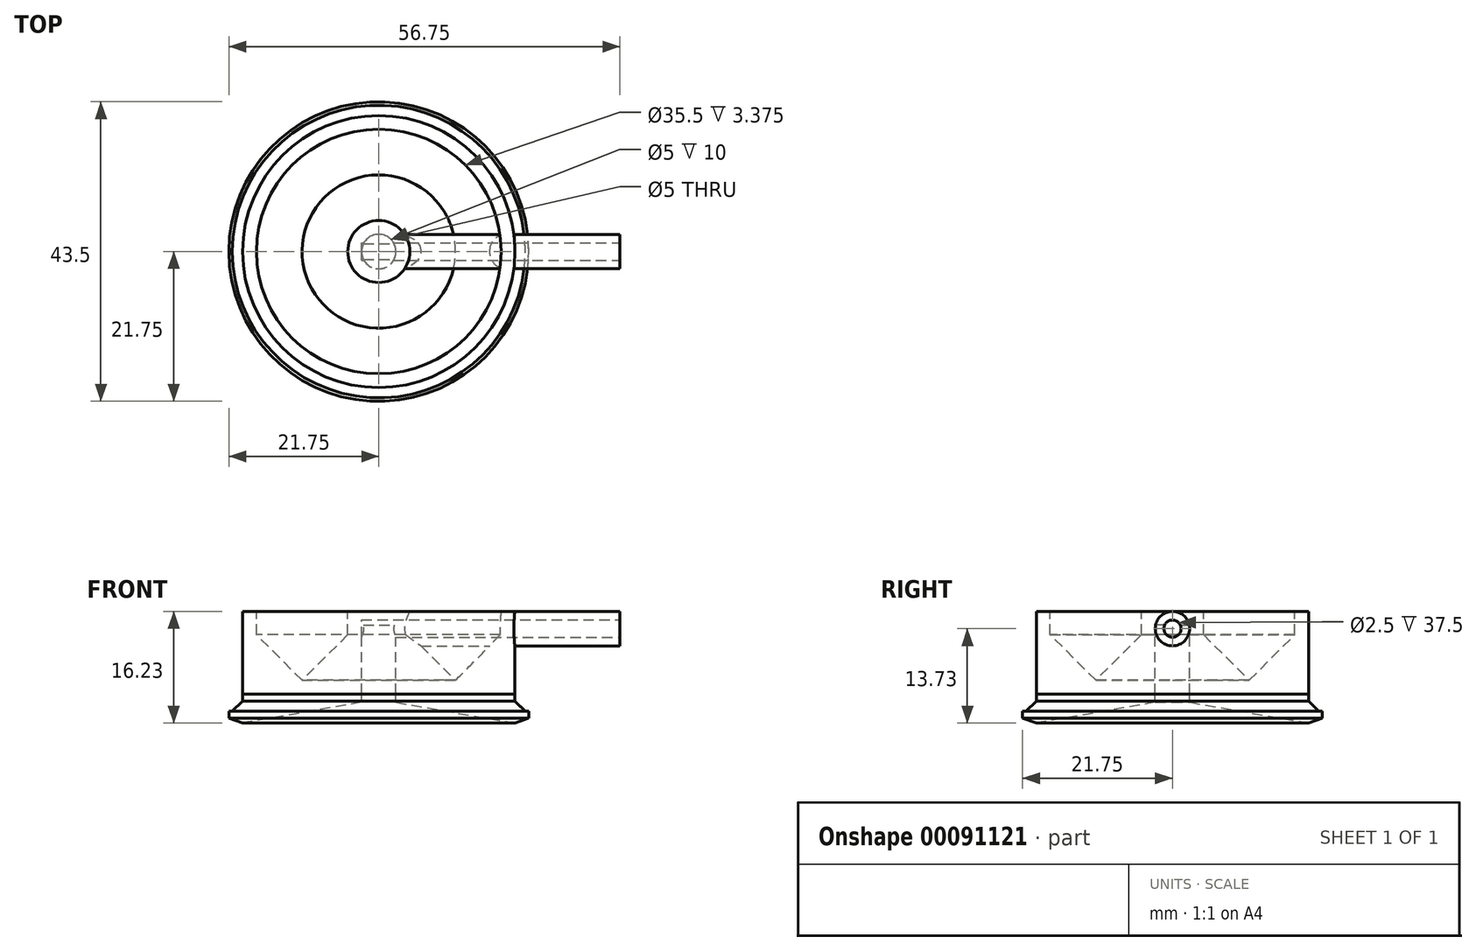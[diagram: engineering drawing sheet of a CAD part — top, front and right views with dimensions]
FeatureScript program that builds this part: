
annotation { "Feature Type Name" : "Feature", "Feature Type Description" : "" }
export const myFeature = defineFeature(function(context is Context, id is Id, definition is map)
    precondition{}
    {
        {
            var Q0;
            Q0=qCreatedBy(makeId("Front.planeOp"),FACE);
            var sketch = newSketch(context, id + "F0", { "sketchPlane" : qUnion([Q0])});
            skLineSegment(sketch, "E0", {"start": v(0, 0) * mm, "end": v(-21.75, 0) * mm, "construction": true});
            skLineSegment(sketch, "E1", {"start": v(-21.75, 0) * mm, "end": v(-21.75, 1) * mm, "construction": true});
            skLineSegment(sketch, "E2", {"start": v(-21.75, 1) * mm, "end": v(-19.75, 1) * mm, "construction": true});
            skLineSegment(sketch, "E3", {"start": v(-19.75, 1) * mm, "end": v(-19.75, 3.5) * mm, "construction": true});
            skLineSegment(sketch, "E4", {"start": v(-19.75, 3.5) * mm, "end": v(-2.5, 3.5) * mm, "construction": true});
            skLineSegment(sketch, "E5", {"start": v(-2.5, 3.5) * mm, "end": v(-2.5, 2.31) * mm, "construction": true});
            skLineSegment(sketch, "E6", {"start": v(-2.5, 2.31) * mm, "end": v(0, 2.31) * mm, "construction": true});
            skLineSegment(sketch, "E7", {"start": v(0, 2.31) * mm, "end": v(0, 0) * mm, "construction": true});
            skLineSegment(sketch, "E8", {"start": v(-2.5, 2.31) * mm, "end": v(-19.75, -0.73) * mm, "construction": true});
            skLineSegment(sketch, "E9", {"start": v(-19.75, -0.73) * mm, "end": v(-21.75, 0) * mm, "construction": true});
            skLineSegment(sketch, "E10", {"start": v(-19.75, 1) * mm, "end": v(-19.75, -0.73) * mm, "construction": true});
            skLineSegment(sketch, "E11", {"start": v(-21.75, 0) * mm, "end": v(-19.75, -0.73) * mm});
            skLineSegment(sketch, "E12", {"start": v(-19.75, -0.73) * mm, "end": v(-2.5, 2.31) * mm});
            skLineSegment(sketch, "E13", {"start": v(-2.5, 2.31) * mm, "end": v(-2.5, 3.5) * mm});
            skLineSegment(sketch, "E14", {"start": v(-2.5, 3.5) * mm, "end": v(-19.75, 3.5) * mm});
            skLineSegment(sketch, "E15", {"start": v(-19.75, 3.5) * mm, "end": v(-19.75, 1) * mm});
            skLineSegment(sketch, "E16", {"start": v(-19.75, 1) * mm, "end": v(-21.75, 1) * mm});
            skLineSegment(sketch, "E17", {"start": v(-21.75, 1) * mm, "end": v(-21.75, 0) * mm});
            skSolve(sketch);
        }
        {
            var Q0;
            Q0=makeQuery(id+"F0.imprint","IMPRINT",FACE,{"disambiguationData":[TD([[makeQuery(id+"F0.imprint","IMPRINT",EDGE,{"derivedFrom":sQuery(id+"F0.wireOp",EDGE,"E11")}),1.0]])]});
            var Q1;
            Q1=sQuery(id+"F0.wireOp",EDGE,"E7");
            revolve(context, id + "F1", {"entities" : qUnion([Q0]), "axis" : qUnion([Q1]), "revolveType" : RevolveType.FULL});
        }
        {
            var Q0;
            Q0=makeQuery(id+"F1.opRevolve","SWEPT_EDGE",EDGE,{"disambiguationData":[OSD([sQuery(id+"F0.wireOp",EDGE,"E15"),sQuery(id+"F0.wireOp",EDGE,"E16")])]});
            chamfer(context, id + "F2", {"entities" : qUnion([Q0]), "chamferType" : ChamferType.OFFSET_ANGLE, "width" : 1.5 * mm, "oppositeDirection" : false, "angle" : 45 * degree, "tangentPropagation" : true});
        }
        {
            var Q0;
            Q0=qCreatedBy(makeId("Front.planeOp"),FACE);
            var sketch = newSketch(context, id + "F3", { "sketchPlane" : qUnion([Q0])});
            skLineSegment(sketch, "E18.bottom", {"start": v(-19.75, 13.5) * mm, "end": v(-2.5, 13.5) * mm, "construction": true});
            skLineSegment(sketch, "E18.top", {"start": v(-19.75, 3.5) * mm, "end": v(-2.5, 3.5) * mm, "construction": true});
            skLineSegment(sketch, "E18.left", {"start": v(-19.75, 13.5) * mm, "end": v(-19.75, 3.5) * mm, "construction": true});
            skLineSegment(sketch, "E18.right", {"start": v(-2.5, 13.5) * mm, "end": v(-2.5, 3.5) * mm, "construction": true});
            skLineSegment(sketch, "E19.bottom", {"start": v(-19.75, 15.5) * mm, "end": v(0, 15.5) * mm, "construction": true});
            skLineSegment(sketch, "E19.top", {"start": v(-19.75, 13.5) * mm, "end": v(0, 13.5) * mm, "construction": true});
            skLineSegment(sketch, "E19.left", {"start": v(-19.75, 15.5) * mm, "end": v(-19.75, 13.5) * mm, "construction": true});
            skLineSegment(sketch, "E19.right", {"start": v(0, 15.5) * mm, "end": v(0, 13.5) * mm, "construction": true});
            skLineSegment(sketch, "E20.bottom", {"start": v(-19.75, 15.5) * mm, "end": v(-17.75, 15.5) * mm, "construction": true});
            skLineSegment(sketch, "E20.top", {"start": v(-19.75, 3.5) * mm, "end": v(-17.75, 3.5) * mm, "construction": true});
            skLineSegment(sketch, "E20.left", {"start": v(-19.75, 15.5) * mm, "end": v(-19.75, 3.5) * mm, "construction": true});
            skLineSegment(sketch, "E20.right", {"start": v(-17.75, 15.5) * mm, "end": v(-17.75, 3.5) * mm, "construction": true});
            skLineSegment(sketch, "E21.bottom", {"start": v(-2.5, 3.5) * mm, "end": v(-4.5, 3.5) * mm, "construction": true});
            skLineSegment(sketch, "E21.top", {"start": v(-2.5, 15.5) * mm, "end": v(-4.5, 15.5) * mm, "construction": true});
            skLineSegment(sketch, "E21.left", {"start": v(-2.5, 3.5) * mm, "end": v(-2.5, 15.5) * mm, "construction": true});
            skLineSegment(sketch, "E21.right", {"start": v(-4.5, 3.5) * mm, "end": v(-4.5, 15.5) * mm, "construction": true});
            skPoint(sketch, "E22", {"position": v(-11.13, 3.5) * mm});
            skLineSegment(sketch, "E23", {"start": v(-19.75, 3.5) * mm, "end": v(-19.75, 15.5) * mm});
            skLineSegment(sketch, "E24", {"start": v(-19.75, 15.5) * mm, "end": v(-17.75, 15.5) * mm});
            skLineSegment(sketch, "E25", {"start": v(-4.5, 15.5) * mm, "end": v(0, 15.5) * mm});
            skLineSegment(sketch, "E26", {"start": v(0, 15.5) * mm, "end": v(0, 13.5) * mm});
            skLineSegment(sketch, "E27", {"start": v(0, 13.5) * mm, "end": v(-2.5, 13.5) * mm});
            skLineSegment(sketch, "E28", {"start": v(-2.5, 13.5) * mm, "end": v(-2.5, 3.5) * mm});
            skLineSegment(sketch, "E29", {"start": v(-2.5, 3.5) * mm, "end": v(-19.75, 3.5) * mm});
            skLineSegment(sketch, "E30.top", {"start": v(-19.75, 5.5) * mm, "end": v(-2.5, 5.5) * mm, "construction": true});
            skLineSegment(sketch, "E30.left", {"start": v(-19.75, 3.5) * mm, "end": v(-19.75, 5.5) * mm, "construction": true});
            skLineSegment(sketch, "E30.right", {"start": v(-2.5, 3.5) * mm, "end": v(-2.5, 5.5) * mm, "construction": true});
            skLineSegment(sketch, "E31", {"start": v(-17.75, 12.12) * mm, "end": v(-11.13, 5.5) * mm, "construction": true});
            skLineSegment(sketch, "E32", {"start": v(-17.75, 12.12) * mm, "end": v(-4.5, 12.12) * mm, "construction": true});
            skLineSegment(sketch, "E33", {"start": v(-4.5, 12.12) * mm, "end": v(-11.13, 5.5) * mm, "construction": true});
            skLineSegment(sketch, "E34", {"start": v(-11.13, 5.5) * mm, "end": v(-11.13, 3.5) * mm, "construction": true});
            skLineSegment(sketch, "E35", {"start": v(-17.75, 15.5) * mm, "end": v(-17.75, 12.12) * mm});
            skLineSegment(sketch, "E36", {"start": v(-17.75, 12.12) * mm, "end": v(-11.13, 5.5) * mm});
            skLineSegment(sketch, "E37", {"start": v(-11.13, 5.5) * mm, "end": v(-4.5, 12.12) * mm});
            skLineSegment(sketch, "E38", {"start": v(-4.5, 12.12) * mm, "end": v(-4.5, 15.5) * mm});
            skSolve(sketch);
        }
        {
            var Q0;
            Q0=makeQuery(id+"F3.imprint","IMPRINT",FACE,{"disambiguationData":[TD([[makeQuery(id+"F3.imprint","IMPRINT",EDGE,{"derivedFrom":sQuery(id+"F3.wireOp",EDGE,"E23")}),-1.0]])]});
            var Q1;
            Q1=sQuery(id+"F3.wireOp",EDGE,"E26");
            revolve(context, id + "F4", {"entities" : qUnion([Q0]), "axis" : qUnion([Q1]), "revolveType" : RevolveType.FULL});
        }
        {
            var Q0;
            Q0=qCreatedBy(makeId("Right.planeOp"),FACE);
            cPlane(context, id + "F5", {"entities" : qUnion([Q0]), "cplaneType" : CPlaneType.OFFSET, "offset" : 25 * mm, "width" : 150 * mm, "height" : 150 * mm});
        }
        {
            var Q0;
            Q0=qCreatedBy(id+"F5.planeOp",FACE);
            var sketch = newSketch(context, id + "F6", { "sketchPlane" : qUnion([Q0])});
            skLineSegment(sketch, "E39", {"start": v(0, 0) * mm, "end": v(0, 15.5) * mm, "construction": true});
            skCircle(sketch, "E40", {"center": v(0, 13) * mm, "radius": 2.5 * mm, "construction": true});
            skCircle(sketch, "E41", {"center": v(0, 13) * mm, "radius": 1.25 * mm, "construction": true});
            skCircle(sketch, "E42", {"center": v(0, 13) * mm, "radius": 2.5 * mm});
            skCircle(sketch, "E43", {"center": v(0, 13) * mm, "radius": 1.25 * mm});
            skSolve(sketch);
        }
        {
            var Q0;
            Q0 = qSketchRegion(id + "F6", true);
            var Q1;
            Q1=makeQuery(id+"F6.imprint","IMPRINT",FACE,{"disambiguationData":[TD([[makeQuery(id+"F6.imprint","IMPRINT",EDGE,{"derivedFrom":sQuery(id+"F6.wireOp",EDGE,"E43")}),1.0]])]});
            var Q2;
            Q2=makeQuery(id+"F4.opRevolve","SWEPT_FACE",FACE,{"disambiguationData":[OSD([sQuery(id+"F3.wireOp",EDGE,"E38")])]});
            extrude(context, id + "F7", {"entities" : qUnion([Q0, Q1]), "operationType" : NewBodyOperationType.ADD, "endBound" : BoundingType.UP_TO_SURFACE, "oppositeDirection" : true, "endBoundEntityFace" : qUnion([Q2]), "depth" : 25 * mm});
        }
        {
            var Q0;
            Q0=makeQuery(id+"F6.imprint","IMPRINT",FACE,{"disambiguationData":[TD([[makeQuery(id+"F6.imprint","IMPRINT",EDGE,{"derivedFrom":sQuery(id+"F6.wireOp",EDGE,"E43")}),1.0]])]});
            extrude(context, id + "F8", {"entities" : qUnion([Q0]), "operationType" : NewBodyOperationType.REMOVE, "oppositeDirection" : true, "depth" : 27.5 * mm});
        }
        {
            var Q0;
            Q0=makeQuery(id+"F6.imprint","IMPRINT",FACE,{"disambiguationData":[TD([[makeQuery(id+"F6.imprint","IMPRINT",EDGE,{"derivedFrom":sQuery(id+"F6.wireOp",EDGE,"E42")}),1.0]])]});
            extrude(context, id + "F9", {"entities" : qUnion([Q0]), "operationType" : NewBodyOperationType.ADD, "depth" : 10 * mm});
        }
    });
